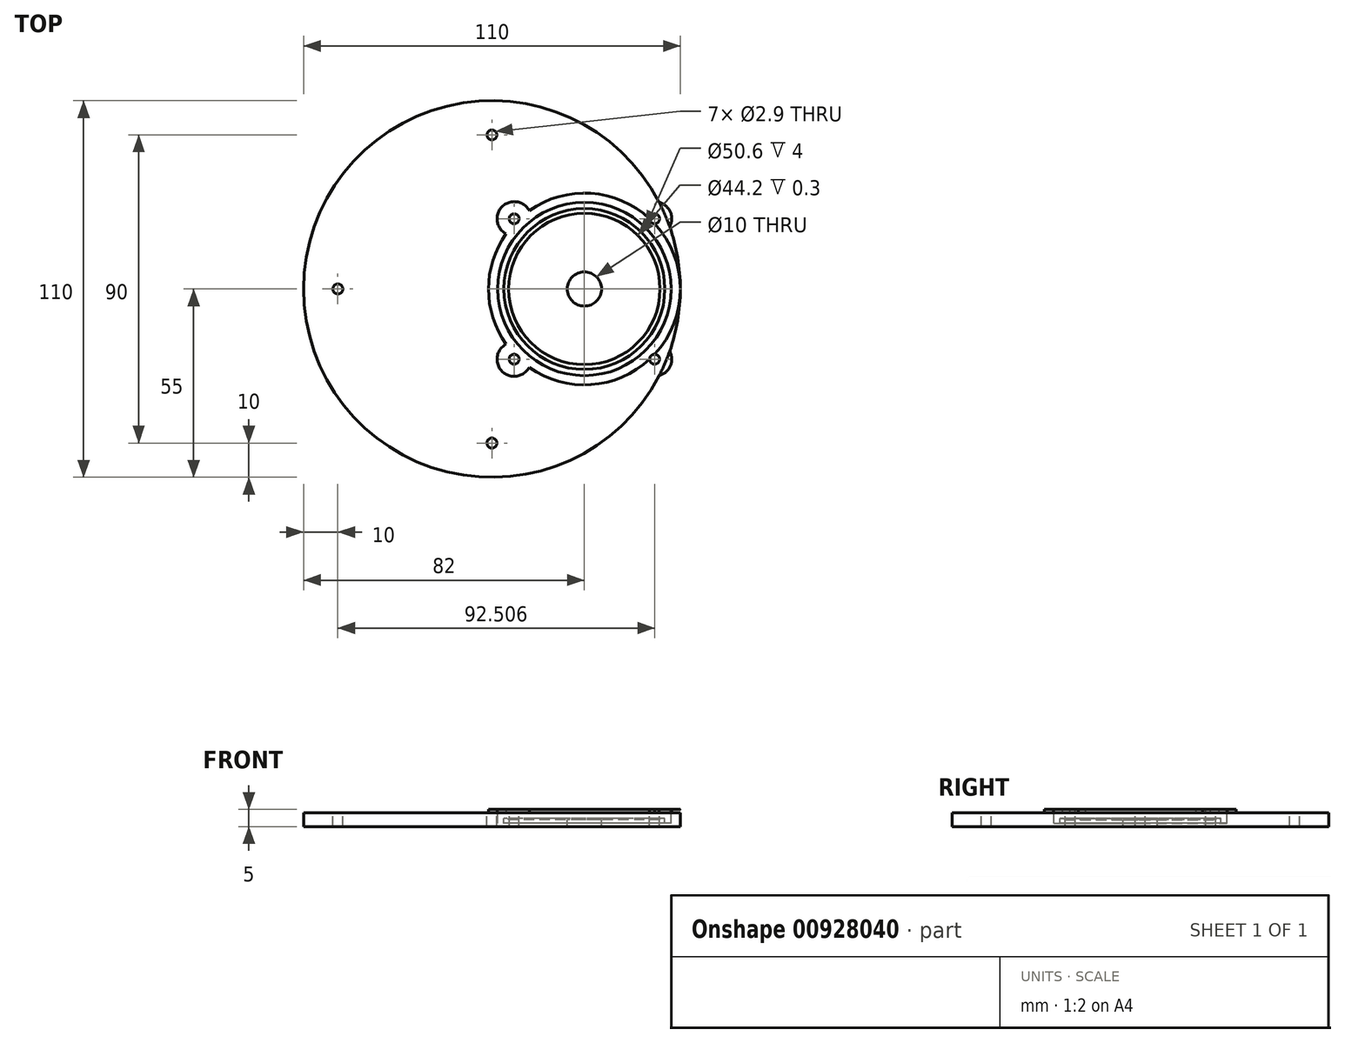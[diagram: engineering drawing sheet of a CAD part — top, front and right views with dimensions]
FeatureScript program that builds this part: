
annotation { "Feature Type Name" : "Feature", "Feature Type Description" : "" }
export const myFeature = defineFeature(function(context is Context, id is Id, definition is map)
    precondition{}
    {
        {
            var Q0;
            Q0=qCreatedBy(makeId("Top.planeOp"),FACE);
            var sketch = newSketch(context, id + "F0", { "sketchPlane" : qUnion([Q0])});
            skCircle(sketch, "E0", {"center": v(0, 0) * mm, "radius": 55 * mm});
            skSolve(sketch);
        }
        {
            var Q0;
            Q0=makeQuery(id+"F0.imprint","IMPRINT",FACE,{"disambiguationData":[TD([[makeQuery(id+"F0.imprint","IMPRINT",EDGE,{"derivedFrom":sQuery(id+"F0.wireOp",EDGE,"E0")}),1.0]])]});
            extrude(context, id + "F1", {"entities" : qUnion([Q0]), "depth" : 4 * mm, "offsetDistance" : 25 * mm});
        }
        {
            var Q0;
            Q0=makeQuery(id+"F1.opExtrude","CAP_FACE",FACE,{"disambiguationData":[OSD([sQuery(id+"F0.wireOp",EDGE,"E0")])],"isStart":false});
            var sketch = newSketch(context, id + "F2", { "sketchPlane" : qUnion([Q0])});
            skCircle(sketch, "E1", {"center": v(27, 0) * mm, "radius": 22.1 * mm});
            skSolve(sketch);
        }
        {
            var Q0;
            Q0=makeQuery(id+"F2.imprint","IMPRINT",FACE,{"disambiguationData":[TD([[makeQuery(id+"F2.imprint","IMPRINT",EDGE,{"derivedFrom":sQuery(id+"F2.wireOp",EDGE,"E1")}),1.0]])]});
            extrude(context, id + "F3", {"entities" : qUnion([Q0]), "operationType" : NewBodyOperationType.REMOVE, "oppositeDirection" : true, "depth" : 2 * mm, "offsetDistance" : 25 * mm});
        }
        {
            var Q0;
            Q0=makeQuery(id+"F1.opExtrude","CAP_FACE",FACE,{"disambiguationData":[OSD([sQuery(id+"F0.wireOp",EDGE,"E0")])],"isStart":false});
            var sketch = newSketch(context, id + "F4", { "sketchPlane" : qUnion([Q0])});
            skCircle(sketch, "E2", {"center": v(27, 0) * mm, "radius": 25.3 * mm});
            skSolve(sketch);
        }
        {
            var Q0;
            Q0=makeQuery(id+"F4.imprint","IMPRINT",FACE,{"disambiguationData":[TD([[makeQuery(id+"F4.imprint","IMPRINT",EDGE,{"derivedFrom":sQuery(id+"F4.wireOp",EDGE,"E2")}),1.0]])]});
            extrude(context, id + "F5", {"entities" : qUnion([Q0]), "operationType" : NewBodyOperationType.REMOVE, "oppositeDirection" : true, "depth" : 1.5 * mm, "offsetDistance" : 25 * mm});
        }
        {
            var Q0;
            Q0=makeQuery(id+"F5.boolean.opBoolean","COPY",FACE,{"derivedFrom":makeQuery(id+"F5.opExtrude","CAP_FACE",FACE,{"disambiguationData":[OSD([sQuery(id+"F2.wireOp",EDGE,"E1"),sQuery(id+"F4.wireOp",EDGE,"E2")])],"isStart":false})});
            var sketch = newSketch(context, id + "F6", { "sketchPlane" : qUnion([Q0])});
            skCircle(sketch, "E3", {"center": v(27, 0) * mm, "radius": 23.5 * mm});
            skSolve(sketch);
        }
        {
            var Q0;
            Q0=makeQuery(id+"F6.imprint","IMPRINT",FACE,{"disambiguationData":[TD([[makeQuery(id+"F6.imprint","IMPRINT",EDGE,{"derivedFrom":sQuery(id+"F6.wireOp",EDGE,"E3")}),-1.0]])]});
            extrude(context, id + "F7", {"entities" : qUnion([Q0]), "operationType" : NewBodyOperationType.REMOVE, "oppositeDirection" : true, "depth" : 1.5 * mm, "offsetDistance" : 25 * mm});
        }
        {
            var Q0;
            Q0=makeQuery(id+"F5.boolean.opBoolean","COPY",FACE,{"derivedFrom":makeQuery(id+"F5.opExtrude","CAP_FACE",FACE,{"disambiguationData":[OSD([sQuery(id+"F2.wireOp",EDGE,"E1"),sQuery(id+"F4.wireOp",EDGE,"E2")])],"isStart":false})});
            extrude(context, id + "F8", {"entities" : qUnion([Q0]), "operationType" : NewBodyOperationType.REMOVE, "oppositeDirection" : true, "depth" : 0.2 * mm, "offsetDistance" : 25 * mm});
        }
        {
            var Q0;
            Q0=makeQuery(id+"F1.opExtrude","CAP_FACE",FACE,{"disambiguationData":[OSD([sQuery(id+"F0.wireOp",EDGE,"E0")])],"isStart":false});
            var sketch = newSketch(context, id + "F9", { "sketchPlane" : qUnion([Q0])});
            skCircle(sketch, "E4", {"center": v(27, 0) * mm, "radius": 28 * mm});
            skSolve(sketch);
        }
        {
            var Q0;
            Q0=makeQuery(id+"F9.imprint","IMPRINT",FACE,{"disambiguationData":[TD([[makeQuery(id+"F9.imprint","IMPRINT",EDGE,{"derivedFrom":sQuery(id+"F9.wireOp",EDGE,"E4")}),1.0]])]});
            extrude(context, id + "F10", {"entities" : qUnion([Q0]), "operationType" : NewBodyOperationType.ADD, "depth" : 1 * mm, "offsetDistance" : 25 * mm});
        }
        {
            var Q0;
            Q0=makeQuery(id+"F3.boolean.opBoolean","COPY",FACE,{"derivedFrom":makeQuery(id+"F3.opExtrude","CAP_FACE",FACE,{"disambiguationData":[OSD([sQuery(id+"F2.wireOp",EDGE,"E1")])],"isStart":false})});
            var sketch = newSketch(context, id + "F11", { "sketchPlane" : qUnion([Q0])});
            skCircle(sketch, "E5", {"center": v(27, 0) * mm, "radius": 5 * mm});
            skSolve(sketch);
        }
        {
            var Q0;
            Q0=makeQuery(id+"F11.imprint","IMPRINT",FACE,{"disambiguationData":[TD([[makeQuery(id+"F11.imprint","IMPRINT",EDGE,{"derivedFrom":sQuery(id+"F11.wireOp",EDGE,"E5")}),1.0]])]});
            extrude(context, id + "F12", {"entities" : qUnion([Q0]), "operationType" : NewBodyOperationType.REMOVE, "oppositeDirection" : true, "depth" : 25 * mm, "offsetDistance" : 25 * mm});
        }
        {
            var Q0;
            Q0=makeQuery(id+"F1.opExtrude","CAP_FACE",FACE,{"disambiguationData":[OSD([sQuery(id+"F0.wireOp",EDGE,"E0")])],"isStart":false});
            var sketch = newSketch(context, id + "F13", { "sketchPlane" : qUnion([Q0])});
            skPoint(sketch, "E6", {"position": v(-2, 0) * mm});
            skPoint(sketch, "E7", {"position": v(27, 0) * mm});
            skCircle(sketch, "E8.1.0", {"center": v(6.5, -20.5) * mm, "radius": 5 * mm});
            skCircle(sketch, "E8.3.0", {"center": v(47.5, -20.5) * mm, "radius": 5 * mm});
            skCircle(sketch, "E9.1.5.0", {"center": v(47.5, 20.5) * mm, "radius": 5 * mm});
            skCircle(sketch, "E9.1.7.0", {"center": v(6.5, 20.5) * mm, "radius": 5 * mm});
            skSolve(sketch);
        }
        {
            var Q0;
            {var subQ0=sQuery(id+"F13.wireOp",EDGE,"E8.1.0");var subQ1=makeQuery(id+"F10.opExtrude","CAP_EDGE",EDGE,{"disambiguationData":[OSD([sQuery(id+"F9.wireOp",EDGE,"E4")])],"isStart":true});var subQ2=makeQuery(id+"F13.imprint","INTERSECT",VERTEX,{"disambiguationData":[OD(0.0)],"derivedFrom":[subQ1,subQ0]});Q0=makeQuery(id+"F13.imprint","IMPRINT",FACE,{"disambiguationData":[TD([[makeQuery(id+"F13.imprint","IMPRINT",EDGE,{"disambiguationData":[TD([[subQ2,1.0]])],"derivedFrom":subQ0}),1.0]])]});}
            var Q1;
            {var subQ0=sQuery(id+"F13.wireOp",EDGE,"E8.3.0");var subQ1=makeQuery(id+"F1.opExtrude","CAP_EDGE",EDGE,{"disambiguationData":[OSD([sQuery(id+"F0.wireOp",EDGE,"E0")])],"isStart":false});var subQ2=makeQuery(id+"F13.imprint","INTERSECT",VERTEX,{"disambiguationData":[OD(0.0)],"derivedFrom":[subQ1,subQ0]});Q1=makeQuery(id+"F13.imprint","IMPRINT",FACE,{"disambiguationData":[TD([[makeQuery(id+"F13.imprint","IMPRINT",EDGE,{"disambiguationData":[TD([[subQ2,1.0]])],"derivedFrom":subQ0}),1.0]])]});}
            var Q2;
            {var subQ0=sQuery(id+"F13.wireOp",EDGE,"E9.1.7.0");var subQ1=makeQuery(id+"F10.opExtrude","CAP_EDGE",EDGE,{"disambiguationData":[OSD([sQuery(id+"F9.wireOp",EDGE,"E4")])],"isStart":true});var subQ2=makeQuery(id+"F13.imprint","INTERSECT",VERTEX,{"disambiguationData":[OD(0.0)],"derivedFrom":[subQ1,subQ0]});Q2=makeQuery(id+"F13.imprint","IMPRINT",FACE,{"disambiguationData":[TD([[makeQuery(id+"F13.imprint","IMPRINT",EDGE,{"disambiguationData":[TD([[subQ2,-1.0]])],"derivedFrom":subQ0}),1.0]])]});}
            var Q3;
            {var subQ0=sQuery(id+"F13.wireOp",EDGE,"E9.1.5.0");var subQ1=makeQuery(id+"F1.opExtrude","CAP_EDGE",EDGE,{"disambiguationData":[OSD([sQuery(id+"F0.wireOp",EDGE,"E0")])],"isStart":false});var subQ2=makeQuery(id+"F13.imprint","INTERSECT",VERTEX,{"disambiguationData":[OD(0.0)],"derivedFrom":[subQ1,subQ0]});Q3=makeQuery(id+"F13.imprint","IMPRINT",FACE,{"disambiguationData":[TD([[makeQuery(id+"F13.imprint","IMPRINT",EDGE,{"disambiguationData":[TD([[subQ2,1.0]])],"derivedFrom":subQ0}),1.0]])]});}
            extrude(context, id + "F14", {"entities" : qUnion([Q0, Q1, Q2, Q3]), "operationType" : NewBodyOperationType.ADD, "depth" : 1 * mm, "offsetDistance" : 25 * mm});
        }
        {
            var Q0;
            {var subQ0=sQuery(id+"F9.wireOp",EDGE,"E4");var subQ1=sQuery(id+"F0.wireOp",EDGE,"E0");Q0=makeQuery(id+"F14.boolean.opBoolean","MERGE",FACE,{"derivedFrom":[makeQuery(id+"F10.opExtrude","CAP_FACE",FACE,{"disambiguationData":[OSD([sQuery(id+"F4.wireOp",EDGE,"E2"),subQ0])],"isStart":false}),makeQuery(id+"F14.opExtrude","CAP_FACE",FACE,{"disambiguationData":[OSD([subQ0,sQuery(id+"F13.wireOp",EDGE,"E8.1.0")])],"isStart":false}),makeQuery(id+"F14.opExtrude","CAP_FACE",FACE,{"disambiguationData":[OSD([subQ1,subQ0,sQuery(id+"F13.wireOp",EDGE,"E8.3.0")])],"isStart":false}),makeQuery(id+"F14.opExtrude","CAP_FACE",FACE,{"disambiguationData":[OSD([subQ1,subQ0,sQuery(id+"F13.wireOp",EDGE,"E9.1.5.0")])],"isStart":false}),makeQuery(id+"F14.opExtrude","CAP_FACE",FACE,{"disambiguationData":[OSD([subQ0,sQuery(id+"F13.wireOp",EDGE,"E9.1.7.0")])],"isStart":false})]});}
            var sketch = newSketch(context, id + "F15", { "sketchPlane" : qUnion([Q0])});
            skCircle(sketch, "E10", {"center": v(6.5, -20.5) * mm, "radius": 1.45 * mm});
            skCircle(sketch, "E11.1.0", {"center": v(47.5, -20.5) * mm, "radius": 1.45 * mm});
            skCircle(sketch, "E11.2.0", {"center": v(47.5, 20.5) * mm, "radius": 1.45 * mm});
            skCircle(sketch, "E11.3.0", {"center": v(6.5, 20.5) * mm, "radius": 1.45 * mm});
            skPoint(sketch, "E11.center", {"position": v(27, 0) * mm});
            skSolve(sketch);
        }
        {
            var Q0;
            Q0=makeQuery(id+"F15.imprint","IMPRINT",FACE,{"disambiguationData":[TD([[makeQuery(id+"F15.imprint","IMPRINT",EDGE,{"derivedFrom":sQuery(id+"F15.wireOp",EDGE,"E11.3.0")}),1.0]])]});
            var Q1;
            Q1=makeQuery(id+"F15.imprint","IMPRINT",FACE,{"disambiguationData":[TD([[makeQuery(id+"F15.imprint","IMPRINT",EDGE,{"derivedFrom":sQuery(id+"F15.wireOp",EDGE,"E11.2.0")}),1.0]])]});
            var Q2;
            Q2=makeQuery(id+"F15.imprint","IMPRINT",FACE,{"disambiguationData":[TD([[makeQuery(id+"F15.imprint","IMPRINT",EDGE,{"derivedFrom":sQuery(id+"F15.wireOp",EDGE,"E11.1.0")}),1.0]])]});
            var Q3;
            Q3=makeQuery(id+"F15.imprint","IMPRINT",FACE,{"disambiguationData":[TD([[makeQuery(id+"F15.imprint","IMPRINT",EDGE,{"derivedFrom":sQuery(id+"F15.wireOp",EDGE,"E10")}),1.0]])]});
            extrude(context, id + "F16", {"entities" : qUnion([Q0, Q1, Q2, Q3]), "operationType" : NewBodyOperationType.REMOVE, "oppositeDirection" : true, "depth" : 25 * mm, "offsetDistance" : 25 * mm});
        }
        {
            var Q0;
            {var subQ1=sQuery(id+"F0.wireOp",EDGE,"E0");Q0=makeQuery(id+"F14.boolean.opBoolean","SPLIT",FACE,{"disambiguationData":[TD([makeQuery(id+"F14.opExtrude","SWEPT_FACE",FACE,{"disambiguationData":[OSD([sQuery(id+"F13.wireOp",EDGE,"E8.1.0")])]})])],"derivedFrom":makeQuery(id+"F1.opExtrude","CAP_FACE",FACE,{"disambiguationData":[OSD([subQ1])],"isStart":false})});}
            var sketch = newSketch(context, id + "F17", { "sketchPlane" : qUnion([Q0])});
            skCircle(sketch, "E12", {"center": v(0, -45) * mm, "radius": 1.45 * mm});
            skCircle(sketch, "E13.1.0", {"center": v(45, 0) * mm, "radius": 1.45 * mm});
            skCircle(sketch, "E13.2.0", {"center": v(0, 45) * mm, "radius": 1.45 * mm});
            skCircle(sketch, "E13.3.0", {"center": v(-45, 0) * mm, "radius": 1.45 * mm});
            skPoint(sketch, "E13.center", {"position": v(0, 0) * mm});
            skSolve(sketch);
        }
        {
            var Q0;
            Q0=makeQuery(id+"F17.imprint","IMPRINT",FACE,{"disambiguationData":[TD([[makeQuery(id+"F17.imprint","IMPRINT",EDGE,{"derivedFrom":sQuery(id+"F17.wireOp",EDGE,"E13.2.0")}),1.0]])]});
            var Q1;
            Q1=makeQuery(id+"F17.imprint","IMPRINT",FACE,{"disambiguationData":[TD([[makeQuery(id+"F17.imprint","IMPRINT",EDGE,{"derivedFrom":sQuery(id+"F17.wireOp",EDGE,"E13.3.0")}),1.0]])]});
            var Q2;
            Q2=makeQuery(id+"F17.imprint","IMPRINT",FACE,{"disambiguationData":[TD([[makeQuery(id+"F17.imprint","IMPRINT",EDGE,{"derivedFrom":sQuery(id+"F17.wireOp",EDGE,"E12")}),1.0]])]});
            extrude(context, id + "F18", {"entities" : qUnion([Q0, Q1, Q2]), "operationType" : NewBodyOperationType.REMOVE, "oppositeDirection" : true, "depth" : 25 * mm, "offsetDistance" : 25 * mm});
        }
    });
